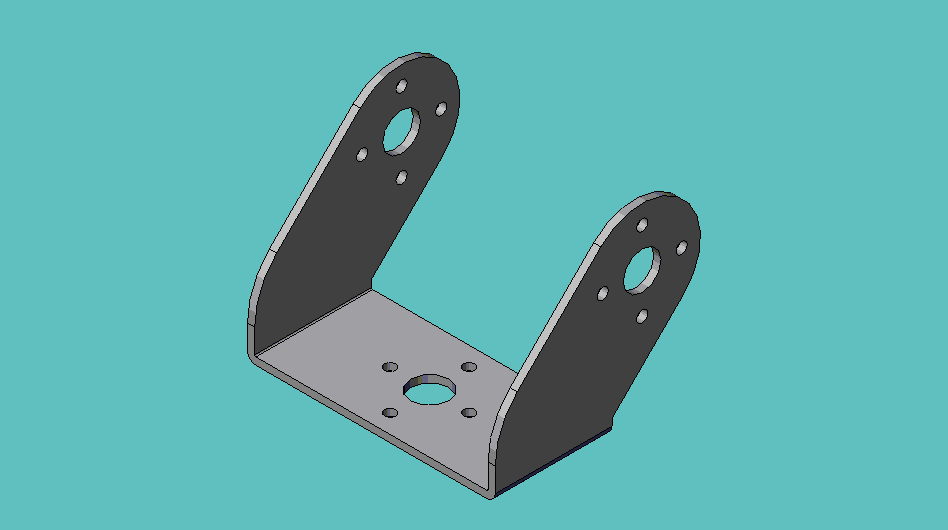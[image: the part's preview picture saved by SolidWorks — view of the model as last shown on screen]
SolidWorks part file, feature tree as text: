
SOLIDWORKS PART (.sldprt)
format: sldprt  version: not decoded by parser v0  size: 300,032 bytes
history: native  units: mm
features: sketch x3, extrude x3, fillet x2, material x1 (+12 scaffold rows collapsed)
feature tree (21):
  scaffold x12  (default folders/planes/origin — collapsed)
  material  "Material <not specified>"
  sketch  "Sketch1"  dims[D1=0.06mm]
  extrude  "Extrude1"  Depth=1.524mm
  sketch  "Sketch4"  dims[D1=25.4mm]
  extrude  "Extrude2"  Depth=1.524mm
  extrude  "Extrude3"  [1 undecoded]
  sketch  "Sketch4<6>"  dims[D1=1.524mm]
  fillet  "Fillet1"  Radius=0.254mm
  fillet  "Fillet2"  Radius=1.778mm
decode coverage: 7 of 8 modeling features carry decoded parameters
note: 1 parameter value undecoded
note: suppression state not decoded; provenance and decode notes live in map.json
